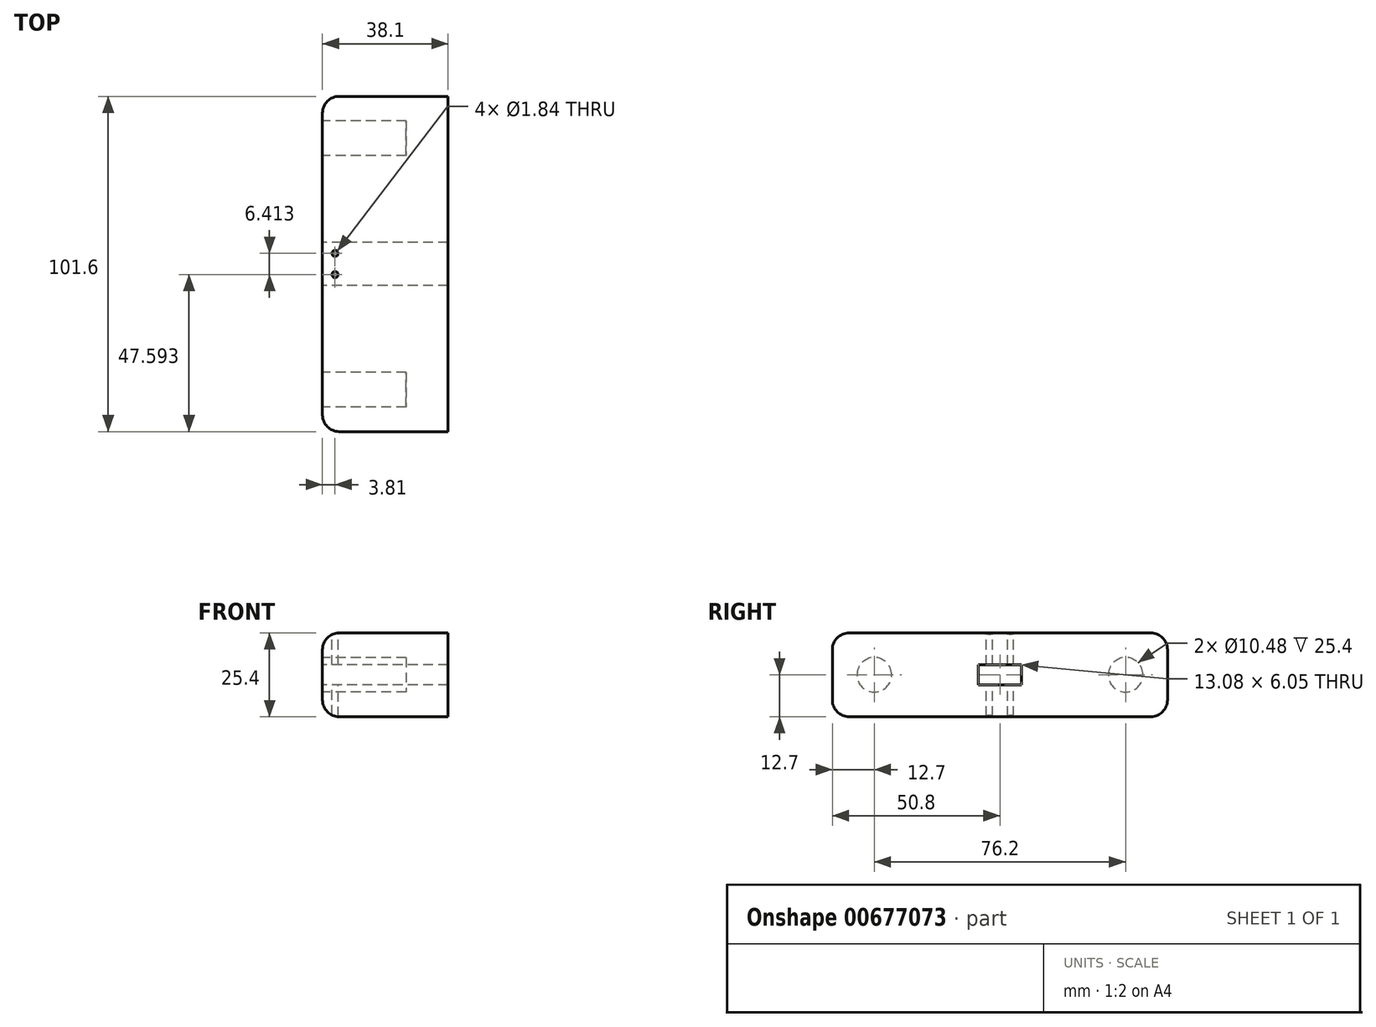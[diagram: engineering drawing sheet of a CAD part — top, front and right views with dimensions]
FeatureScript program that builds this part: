
annotation { "Feature Type Name" : "Feature", "Feature Type Description" : "" }
export const myFeature = defineFeature(function(context is Context, id is Id, definition is map)
    precondition{}
    {
        {
            var Q0;
            Q0=qCreatedBy(makeId("Top.planeOp"),FACE);
            var sketch = newSketch(context, id + "F0", { "sketchPlane" : qUnion([Q0])});
            skLineSegment(sketch, "E0.bottom", {"start": v(19.05, 50.8) * mm, "end": v(-19.05, 50.8) * mm});
            skLineSegment(sketch, "E0.top", {"start": v(19.05, -50.8) * mm, "end": v(-19.05, -50.8) * mm});
            skLineSegment(sketch, "E0.left", {"start": v(19.05, 50.8) * mm, "end": v(19.05, -50.8) * mm});
            skLineSegment(sketch, "E0.right", {"start": v(-19.05, 50.8) * mm, "end": v(-19.05, -50.8) * mm});
            skPoint(sketch, "E0.middle", {"position": v(0, 0) * mm});
            skSolve(sketch);
        }
        {
            var Q0;
            Q0 = qSketchRegion(id + "F0", true);
            extrude(context, id + "F1", {"entities" : qUnion([Q0]), "endBound" : BoundingType.SYMMETRIC, "depth" : 25.4 * mm, "offsetDistance" : 25.4 * mm});
        }
        {
            var Q0;
            Q0=makeQuery(id+"F1.opExtrude","SWEPT_FACE",FACE,{"disambiguationData":[OSD([sQuery(id+"F0.wireOp",EDGE,"E0.right")])]});
            var sketch = newSketch(context, id + "F2", { "sketchPlane" : qUnion([Q0])});
            skCircle(sketch, "E1", {"center": v(38.1, 0) * mm, "radius": 5.24 * mm});
            skLineSegment(sketch, "E2", {"start": v(38.1, 0) * mm, "end": v(0, 0) * mm, "construction": true});
            skCircle(sketch, "E3.MirrorC", {"center": v(-38.1, 0) * mm, "radius": 5.24 * mm});
            skSolve(sketch);
        }
        {
            var Q0;
            Q0 = qSketchRegion(id + "F2", true);
            extrude(context, id + "F3", {"entities" : qUnion([Q0]), "operationType" : NewBodyOperationType.REMOVE, "oppositeDirection" : true, "depth" : 25.4 * mm, "offsetDistance" : 25.4 * mm});
        }
        {
            var Q0;
            Q0=makeQuery(id+"F1.opExtrude","CAP_EDGE",EDGE,{"disambiguationData":[OSD([sQuery(id+"F0.wireOp",EDGE,"E0.bottom")])],"isStart":false});
            var Q1;
            Q1=makeQuery(id+"F1.opExtrude","CAP_EDGE",EDGE,{"disambiguationData":[OSD([sQuery(id+"F0.wireOp",EDGE,"E0.right")])],"isStart":false});
            var Q2;
            Q2=makeQuery(id+"F1.opExtrude","SWEPT_EDGE",EDGE,{"disambiguationData":[OSD([sQuery(id+"F0.wireOp",EDGE,"E0.bottom"),sQuery(id+"F0.wireOp",EDGE,"E0.right")])]});
            var Q3;
            Q3=makeQuery(id+"F1.opExtrude","SWEPT_EDGE",EDGE,{"disambiguationData":[OSD([sQuery(id+"F0.wireOp",EDGE,"E0.top"),sQuery(id+"F0.wireOp",EDGE,"E0.right")])]});
            var Q4;
            Q4=makeQuery(id+"F1.opExtrude","CAP_EDGE",EDGE,{"disambiguationData":[OSD([sQuery(id+"F0.wireOp",EDGE,"E0.right")])],"isStart":true});
            var Q5;
            Q5=makeQuery(id+"F1.opExtrude","CAP_EDGE",EDGE,{"disambiguationData":[OSD([sQuery(id+"F0.wireOp",EDGE,"E0.bottom")])],"isStart":true});
            var Q6;
            Q6=makeQuery(id+"F1.opExtrude","CAP_EDGE",EDGE,{"disambiguationData":[OSD([sQuery(id+"F0.wireOp",EDGE,"E0.top")])],"isStart":true});
            var Q7;
            Q7=makeQuery(id+"F1.opExtrude","CAP_EDGE",EDGE,{"disambiguationData":[OSD([sQuery(id+"F0.wireOp",EDGE,"E0.top")])],"isStart":false});
            fillet(context, id + "F4", {"entities" : qUnion([Q0, Q1, Q2, Q3, Q4, Q5, Q6, Q7]), "radius" : 5.08 * mm, "tangentPropagation" : true, "allowEdgeOverflow" : false});
        }
        {
            var Q0;
            Q0=makeQuery(id+"F1.opExtrude","SWEPT_FACE",FACE,{"disambiguationData":[OSD([sQuery(id+"F0.wireOp",EDGE,"E0.right")])]});
            var sketch = newSketch(context, id + "F5", { "sketchPlane" : qUnion([Q0])});
            skLineSegment(sketch, "E4.bottom", {"start": v(6.54, -3.02) * mm, "end": v(-6.54, -3.02) * mm});
            skLineSegment(sketch, "E4.top", {"start": v(6.54, 3.02) * mm, "end": v(-6.54, 3.02) * mm});
            skLineSegment(sketch, "E4.left", {"start": v(6.54, -3.02) * mm, "end": v(6.54, 3.02) * mm});
            skLineSegment(sketch, "E4.right", {"start": v(-6.54, -3.02) * mm, "end": v(-6.54, 3.02) * mm});
            skPoint(sketch, "E4.middle", {"position": v(0, 0) * mm});
            skSolve(sketch);
        }
        {
            var Q0;
            Q0 = qSketchRegion(id + "F5", true);
            extrude(context, id + "F6", {"entities" : qUnion([Q0]), "operationType" : NewBodyOperationType.REMOVE, "endBound" : BoundingType.UP_TO_NEXT, "oppositeDirection" : true, "depth" : 25.4 * mm, "offsetDistance" : 25.4 * mm});
        }
        {
            var Q0;
            Q0=makeQuery(id+"F1.opExtrude","CAP_FACE",FACE,{"disambiguationData":[OSD([sQuery(id+"F0.wireOp",EDGE,"E0.bottom"),sQuery(id+"F0.wireOp",EDGE,"E0.top"),sQuery(id+"F0.wireOp",EDGE,"E0.left"),sQuery(id+"F0.wireOp",EDGE,"E0.right")])],"isStart":false});
            var sketch = newSketch(context, id + "F7", { "sketchPlane" : qUnion([Q0])});
            skLineSegment(sketch, "E5", {"start": v(-15.24, -3.2) * mm, "end": v(-15.24, 3.2) * mm});
            skCircle(sketch, "E6", {"center": v(-15.24, 3.2) * mm, "radius": 0.92 * mm});
            skCircle(sketch, "E7", {"center": v(-15.24, -3.2) * mm, "radius": 0.92 * mm});
            skLineSegment(sketch, "E8", {"start": v(-15.24, 0) * mm, "end": v(-19.05, 0) * mm});
            skSolve(sketch);
        }
        {
            var Q0;
            Q0=makeQuery(id+"F7.imprint","IMPRINT",FACE,{"disambiguationData":[TD([[makeQuery(id+"F7.imprint","IMPRINT",EDGE,{"derivedFrom":sQuery(id+"F7.wireOp",EDGE,"E7")}),1.0]])]});
            var Q1;
            Q1=makeQuery(id+"F7.imprint","IMPRINT",FACE,{"disambiguationData":[TD([[makeQuery(id+"F7.imprint","IMPRINT",EDGE,{"derivedFrom":sQuery(id+"F7.wireOp",EDGE,"E6")}),1.0]])]});
            extrude(context, id + "F8", {"entities" : qUnion([Q0, Q1]), "operationType" : NewBodyOperationType.REMOVE, "endBound" : BoundingType.THROUGH_ALL, "oppositeDirection" : true, "depth" : 25.4 * mm, "offsetDistance" : 25.4 * mm});
        }
    });
